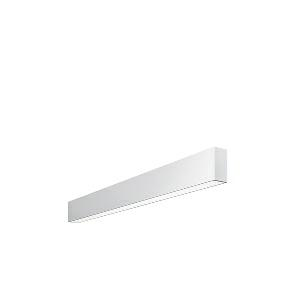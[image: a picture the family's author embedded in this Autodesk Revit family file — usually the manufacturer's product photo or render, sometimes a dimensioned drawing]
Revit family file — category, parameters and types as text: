
# Revit family: idoo_line_-_ilw_2000_830_d_00808326_d90b
name_source: partatom
category: Lighting Fixtures
units: mm (PartAtom-declared; Revit-internal decimal feet)

## family parameters
Cut with Voids When Loaded = No
Host = Face
Light Source = No
Part Type = Normal
Room Calculation Point = No
Round Connector Dimension = Use Diameter
Shared = No

## types (1)
- IDOO.line - ILW 2000/830/D (1 x LED, 2250 lm, 3000K)
    Apparent Load = 17 VA
    Approval mark = CE
    CIE Flux Codes = 66 91 98 40 100
    Color Rendering = 80-89
    Color Temperature = 3000K
    Control Gear = Electronic ballast
    Default Elevation = 2000 mm  [stored 6.56168 ft]
    Description = ILW 2000/830/D|Wall-mounted luminaire|light source:  |work equipment: Adjustable electronic ballast, digital DALI|connected load: 220-240V, 50/60Hz|Power consumption: approx. 17 W|standby: approx. 0,25|power factor: approx. 0,970|luminous flux: 2250 lm|luminous efficacy: 132 lm/W|light distribution: Direct/indirect|direct ratio: approx. 40 %|colour temperature: Warm white, ca. 3000 K|color rendering index (CRI): >= 80|chromaticity tolerance:  3 SDCM|technology: Continuously dimmable|operation: External|luminaire body|material: Sectional aluminium|colour: White|lamp cover: Acrylic (PMMA), Clear|weight (net): approx. 3.9 kg|mains lead: Connector|design: Mounted version|Fastening: Mounting rail|glare control: Prism aperture|luminance(L65): <= 2700 cd/m|unified glare rating(4H 8H): <=  16|special features: DALI Load 1x, TouchDIM - dimming via standard switch, Flicker-free, Suitable as emergency lighting|
    Frequency = 50 Hz
    Height = 110 mm
    Lamp = 1 x LED
    Lamp Light Flux = 2250 lm
    Lamp count = 1
    Length = 854 mm
    Luminous efficacy = 132 lm/W
    Manufacturer = Waldmann
    ModVariant = No
    Model = 00808326
    Mounting Place = Wall
    Mounting Type = Surface mounted
    Number of Poles = 1
    OnlyDefault = Yes
    Power Factor = 1
    Product Name = IDOO.line - ILW 2000/830/D
    Product group = Wall mounted Luminaire
    ProductGroupID = 20
    Protection Class = Protection class I
    Protection Degree = IP 40
    RLX_Detail_Level = 1
    RLX_Emergency_Light_Flux = 0 lm
    RLX_Emergency_Type = 0
    RLX_Emergency_Type_DB = No
    RlxData = <blob elided: 31621 chars, md5=709389f4>
    Socket = socket
    Standby Power = 0 W
    System Light Flux = 2250 lm
    System Power = 17 W
    Type Comments = Product without accessories
    Type Image = 113966000-00757945.jpg
    URL = http://relux.com
    VarID = ---
    Voltage = 230 V
    Voltage Range = 220-240 V
    Weight = 0.00 kg
    Width = 60 mm  [stored 0.19685 ft]

note: [stored X ft] marks values corroborated as IEEE doubles in the binary element streams (Revit-internal decimal feet)

## geometry (parser evidence)
native form markers: Blend x4, Sweep x13
no freeform markers — native parametric forms only
